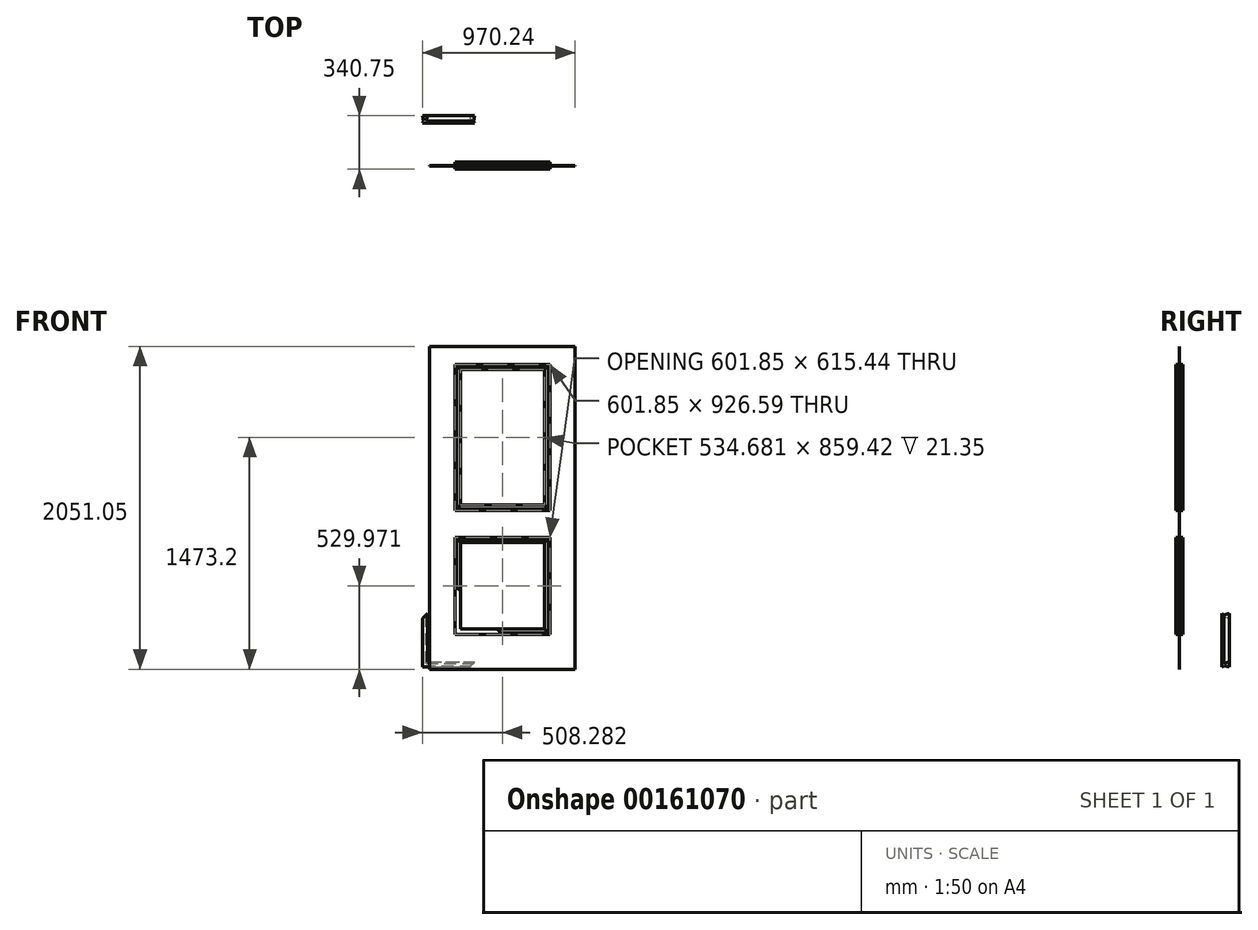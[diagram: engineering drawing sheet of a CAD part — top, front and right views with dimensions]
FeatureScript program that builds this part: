
annotation { "Feature Type Name" : "Feature", "Feature Type Description" : "" }
export const myFeature = defineFeature(function(context is Context, id is Id, definition is map)
    precondition{}
    {
        {
            var Q0;
            Q0=qCreatedBy(makeId("Front.planeOp"),FACE);
            var sketch = newSketch(context, id + "F0", { "sketchPlane" : qUnion([Q0])});
            skLineSegment(sketch, "E0.bottom", {"start": v(0, 0) * mm, "end": v(923.92, 0) * mm});
            skLineSegment(sketch, "E0.top", {"start": v(0, 2051.05) * mm, "end": v(923.92, 2051.05) * mm});
            skLineSegment(sketch, "E0.left", {"start": v(0, 0) * mm, "end": v(0, 2051.05) * mm});
            skLineSegment(sketch, "E0.right", {"start": v(923.93, 0) * mm, "end": v(923.92, 2051.05) * mm});
            skLineSegment(sketch, "E1.bottom", {"start": v(762.89, 1936.5) * mm, "end": v(161.04, 1936.5) * mm});
            skLineSegment(sketch, "E1.top", {"start": v(762.89, 1009.9) * mm, "end": v(161.04, 1009.9) * mm});
            skLineSegment(sketch, "E1.left", {"start": v(762.89, 1936.5) * mm, "end": v(762.89, 1009.9) * mm});
            skLineSegment(sketch, "E1.right", {"start": v(161.04, 1936.5) * mm, "end": v(161.04, 1009.9) * mm});
            skLineSegment(sketch, "E2.bottom", {"start": v(161.04, 837.7) * mm, "end": v(762.89, 837.7) * mm});
            skLineSegment(sketch, "E2.top", {"start": v(161.04, 222.25) * mm, "end": v(762.89, 222.25) * mm});
            skLineSegment(sketch, "E2.left", {"start": v(161.04, 837.7) * mm, "end": v(161.04, 222.25) * mm});
            skLineSegment(sketch, "E2.right", {"start": v(762.89, 837.7) * mm, "end": v(762.89, 222.25) * mm});
            skSolve(sketch);
        }
        {
            var Q0;
            Q0=qSketchRegion(id+"F0",true);
            extrude(context, id + "F1", {"entities" : qUnion([Q0]), "depth" : ((1 + 3 / 4) / 2) * mm, "hasSecondDirection" : true, "secondDirectionOppositeDirection" : true, "secondDirectionDepth" : ((1 + 3 / 4) / 2) * mm});
        }
        {
            var Q0;
            Q0=qCreatedBy(makeId("Front.planeOp"),FACE);
            var sketch = newSketch(context, id + "F2", { "sketchPlane" : qUnion([Q0])});
            skLineSegment(sketch, "E3.0", {"start": v(762.89, 837.7) * mm, "end": v(762.89, 222.25) * mm});
            skLineSegment(sketch, "E4.0", {"start": v(161.04, 222.25) * mm, "end": v(762.89, 222.25) * mm});
            skLineSegment(sketch, "E5.0", {"start": v(161.04, 837.7) * mm, "end": v(161.04, 222.25) * mm});
            skLineSegment(sketch, "E6.0", {"start": v(161.04, 837.7) * mm, "end": v(762.89, 837.7) * mm});
            skLineSegment(sketch, "E7.0", {"start": v(762.89, 1009.9) * mm, "end": v(161.04, 1009.9) * mm});
            skLineSegment(sketch, "E8.0", {"start": v(762.89, 1936.5) * mm, "end": v(762.89, 1009.9) * mm});
            skLineSegment(sketch, "E9.0", {"start": v(161.04, 1936.5) * mm, "end": v(161.04, 1009.9) * mm});
            skLineSegment(sketch, "E10.0", {"start": v(762.89, 1936.5) * mm, "end": v(161.04, 1936.5) * mm});
            skLineSegment(sketch, "E11", {"start": v(461.96, 1936.5) * mm, "end": v(461.96, 222.25) * mm});
            skLineSegment(sketch, "E12", {"start": v(161.04, 1473.2) * mm, "end": v(762.89, 1473.2) * mm});
            skLineSegment(sketch, "E13", {"start": v(161.04, 529.97) * mm, "end": v(762.89, 529.97) * mm});
            skLineSegment(sketch, "E14", {"start": v(161.04, 1936.5) * mm, "end": v(186.44, 1911.1) * mm});
            skLineSegment(sketch, "E15", {"start": v(161.04, 837.7) * mm, "end": v(186.44, 812.3) * mm});
            skLineSegment(sketch, "E16", {"start": v(762.89, 1936.5) * mm, "end": v(737.49, 1911.1) * mm});
            skLineSegment(sketch, "E17", {"start": v(161.04, 1009.9) * mm, "end": v(186.44, 1035.3) * mm});
            skLineSegment(sketch, "E18", {"start": v(762.89, 1009.9) * mm, "end": v(737.49, 1035.3) * mm});
            skLineSegment(sketch, "E19", {"start": v(762.89, 222.25) * mm, "end": v(737.49, 247.65) * mm});
            skLineSegment(sketch, "E20", {"start": v(762.89, 837.7) * mm, "end": v(737.49, 812.3) * mm});
            skLineSegment(sketch, "E21", {"start": v(161.04, 222.25) * mm, "end": v(186.44, 247.65) * mm});
            skSolve(sketch);
        }
        {
            var Q0;
            Q0=qCreatedBy(makeId("Front.planeOp"),FACE);
            var sketch = newSketch(context, id + "F3", { "sketchPlane" : qUnion([Q0])});
            skPoint(sketch, "E22.0", {"position": v(161.04, 1473.2) * mm});
            skPoint(sketch, "E23.0", {"position": v(762.89, 1473.2) * mm});
            skPoint(sketch, "E24.0", {"position": v(461.96, 1936.5) * mm});
            skLineSegment(sketch, "E25.0", {"start": v(461.96, 1936.5) * mm, "end": v(461.96, 222.25) * mm});
            skPoint(sketch, "E26.0", {"position": v(762.89, 1009.9) * mm});
            skPoint(sketch, "E27.0", {"position": v(161.04, 1009.9) * mm});
            skPoint(sketch, "E28.0", {"position": v(762.89, 1936.5) * mm});
            skPoint(sketch, "E29.0", {"position": v(161.04, 1936.5) * mm});
            skPoint(sketch, "E30.0", {"position": v(161.04, 837.7) * mm});
            skPoint(sketch, "E31.0", {"position": v(762.89, 837.7) * mm});
            skPoint(sketch, "E32.0", {"position": v(762.89, 529.97) * mm});
            skPoint(sketch, "E33.0", {"position": v(762.89, 222.25) * mm});
            skPoint(sketch, "E34.0", {"position": v(161.04, 222.25) * mm});
            skPoint(sketch, "E35.0", {"position": v(161.04, 529.97) * mm});
            skLineSegment(sketch, "E36", {"start": v(161.04, 837.7) * mm, "end": v(461.96, 837.7) * mm});
            skLineSegment(sketch, "E37", {"start": v(461.96, 837.7) * mm, "end": v(762.89, 837.7) * mm});
            skLineSegment(sketch, "E38", {"start": v(762.89, 837.7) * mm, "end": v(762.89, 529.97) * mm});
            skLineSegment(sketch, "E39", {"start": v(762.89, 529.97) * mm, "end": v(762.89, 222.25) * mm});
            skLineSegment(sketch, "E40", {"start": v(762.89, 222.25) * mm, "end": v(461.96, 222.25) * mm});
            skLineSegment(sketch, "E41", {"start": v(461.96, 222.25) * mm, "end": v(161.04, 222.25) * mm});
            skLineSegment(sketch, "E42", {"start": v(161.04, 222.25) * mm, "end": v(161.04, 529.97) * mm});
            skLineSegment(sketch, "E43", {"start": v(161.04, 529.97) * mm, "end": v(161.04, 837.7) * mm});
            skLineSegment(sketch, "E44", {"start": v(161.04, 1936.5) * mm, "end": v(461.96, 1936.5) * mm});
            skLineSegment(sketch, "E45", {"start": v(461.96, 1936.5) * mm, "end": v(762.89, 1936.5) * mm});
            skLineSegment(sketch, "E46", {"start": v(762.89, 1936.5) * mm, "end": v(762.89, 1473.2) * mm});
            skLineSegment(sketch, "E47", {"start": v(762.89, 1473.2) * mm, "end": v(762.89, 1009.9) * mm});
            skLineSegment(sketch, "E48", {"start": v(762.89, 1009.9) * mm, "end": v(461.96, 1009.9) * mm});
            skLineSegment(sketch, "E49", {"start": v(461.96, 1009.9) * mm, "end": v(161.04, 1009.9) * mm});
            skLineSegment(sketch, "E50", {"start": v(161.04, 1009.9) * mm, "end": v(161.04, 1473.2) * mm});
            skLineSegment(sketch, "E51", {"start": v(161.04, 1473.2) * mm, "end": v(161.04, 1936.5) * mm});
            skSolve(sketch);
        }
        {
            var Q0;
            Q0=sQuery(id+"F2.wireOp",VERTEX,"E14.end");
            var Q1;
            Q1=sQuery(id+"F3.wireOp",VERTEX,"E29.0");
            var Q2;
            Q2=makeQuery(id+"F1.opExtrude","CAP_VERTEX",VERTEX,{"disambiguationData":[OSD([sQuery(id+"F0.wireOp",EDGE,"E1.bottom"),sQuery(id+"F0.wireOp",EDGE,"E1.right")])],"isStart":false});
            cPlane(context, id + "F4", {"entities" : qUnion([Q0, Q1, Q2]), "cplaneType" : CPlaneType.THREE_POINT, "offset" : 25.4 * mm, "width" : 152.4 * mm, "height" : 152.4 * mm});
        }
        {
            var Q0;
            Q0=sQuery(id+"F3.wireOp",VERTEX,"E28.0");
            var Q1;
            Q1=sQuery(id+"F2.wireOp",VERTEX,"E16.end");
            var Q2;
            Q2=makeQuery(id+"F1.opExtrude","CAP_VERTEX",VERTEX,{"disambiguationData":[OSD([sQuery(id+"F0.wireOp",EDGE,"E1.bottom"),sQuery(id+"F0.wireOp",EDGE,"E1.left")])],"isStart":false});
            cPlane(context, id + "F5", {"entities" : qUnion([Q0, Q1, Q2]), "cplaneType" : CPlaneType.THREE_POINT, "offset" : 25.4 * mm, "width" : 152.4 * mm, "height" : 152.4 * mm});
        }
        {
            var Q0;
            Q0=sQuery(id+"F3.wireOp",VERTEX,"E26.0");
            var Q1;
            Q1=sQuery(id+"F2.wireOp",VERTEX,"E18.end");
            var Q2;
            Q2=makeQuery(id+"F1.opExtrude","CAP_VERTEX",VERTEX,{"disambiguationData":[OSD([sQuery(id+"F0.wireOp",EDGE,"E1.top"),sQuery(id+"F0.wireOp",EDGE,"E1.left")])],"isStart":false});
            cPlane(context, id + "F6", {"entities" : qUnion([Q0, Q1, Q2]), "cplaneType" : CPlaneType.THREE_POINT, "offset" : 25.4 * mm, "width" : 152.4 * mm, "height" : 152.4 * mm});
        }
        {
            var Q0;
            Q0=sQuery(id+"F3.wireOp",VERTEX,"E27.0");
            var Q1;
            Q1=sQuery(id+"F2.wireOp",VERTEX,"E17.end");
            var Q2;
            Q2=makeQuery(id+"F1.opExtrude","CAP_VERTEX",VERTEX,{"disambiguationData":[OSD([sQuery(id+"F0.wireOp",EDGE,"E1.top"),sQuery(id+"F0.wireOp",EDGE,"E1.right")])],"isStart":false});
            cPlane(context, id + "F7", {"entities" : qUnion([Q0, Q1, Q2]), "cplaneType" : CPlaneType.THREE_POINT, "offset" : 25.4 * mm, "width" : 152.4 * mm, "height" : 152.4 * mm});
        }
        {
            var Q0;
            Q0=sQuery(id+"F2.wireOp",VERTEX,"E15.end");
            var Q1;
            Q1=sQuery(id+"F3.wireOp",VERTEX,"E30.0");
            var Q2;
            Q2=makeQuery(id+"F1.opExtrude","CAP_VERTEX",VERTEX,{"disambiguationData":[OSD([sQuery(id+"F0.wireOp",EDGE,"E2.bottom"),sQuery(id+"F0.wireOp",EDGE,"E2.left")])],"isStart":false});
            cPlane(context, id + "F8", {"entities" : qUnion([Q0, Q1, Q2]), "cplaneType" : CPlaneType.THREE_POINT, "offset" : 25.4 * mm, "width" : 152.4 * mm, "height" : 152.4 * mm});
        }
        {
            var Q0;
            Q0=sQuery(id+"F2.wireOp",VERTEX,"E21.end");
            var Q1;
            Q1=sQuery(id+"F3.wireOp",VERTEX,"E34.0");
            var Q2;
            Q2=makeQuery(id+"F1.opExtrude","CAP_VERTEX",VERTEX,{"disambiguationData":[OSD([sQuery(id+"F0.wireOp",EDGE,"E2.top"),sQuery(id+"F0.wireOp",EDGE,"E2.left")])],"isStart":false});
            cPlane(context, id + "F9", {"entities" : qUnion([Q0, Q1, Q2]), "cplaneType" : CPlaneType.THREE_POINT, "offset" : 25.4 * mm, "width" : 152.4 * mm, "height" : 152.4 * mm});
        }
        {
            var Q0;
            Q0=sQuery(id+"F2.wireOp",VERTEX,"E19.end");
            var Q1;
            Q1=sQuery(id+"F3.wireOp",VERTEX,"E33.0");
            var Q2;
            Q2=makeQuery(id+"F1.opExtrude","CAP_VERTEX",VERTEX,{"disambiguationData":[OSD([sQuery(id+"F0.wireOp",EDGE,"E2.top"),sQuery(id+"F0.wireOp",EDGE,"E2.right")])],"isStart":false});
            cPlane(context, id + "F10", {"entities" : qUnion([Q0, Q1, Q2]), "cplaneType" : CPlaneType.THREE_POINT, "offset" : 25.4 * mm, "width" : 152.4 * mm, "height" : 152.4 * mm});
        }
        {
            var Q0;
            Q0=sQuery(id+"F3.wireOp",VERTEX,"E31.0");
            var Q1;
            Q1=sQuery(id+"F2.wireOp",VERTEX,"E20.end");
            var Q2;
            Q2=makeQuery(id+"F1.opExtrude","CAP_VERTEX",VERTEX,{"disambiguationData":[OSD([sQuery(id+"F0.wireOp",EDGE,"E2.bottom"),sQuery(id+"F0.wireOp",EDGE,"E2.right")])],"isStart":false});
            cPlane(context, id + "F11", {"entities" : qUnion([Q0, Q1, Q2]), "cplaneType" : CPlaneType.THREE_POINT, "offset" : 25.4 * mm, "width" : 152.4 * mm, "height" : 152.4 * mm});
        }
        {
            var Q0;
            Q0=makeQuery(id+"F1.opExtrude","SWEPT_FACE",FACE,{"disambiguationData":[OSD([sQuery(id+"F0.wireOp",EDGE,"E2.top")])]});
            var sketch = newSketch(context, id + "F12", { "sketchPlane" : qUnion([Q0])});
            skLineSegment(sketch, "E52.0", {"start": v(161.04, -22.23) * mm, "end": v(161.04, 22.23) * mm});
            skLineSegment(sketch, "E53.0", {"start": v(762.89, -22.23) * mm, "end": v(762.89, 22.23) * mm});
            skLineSegment(sketch, "E54", {"start": v(161.04, -22.22) * mm, "end": v(179, -11.3) * mm});
            skLineSegment(sketch, "E55", {"start": v(179, -11.3) * mm, "end": v(228.2, -22.23) * mm});
            skLineSegment(sketch, "E56", {"start": v(228.2, -22.23) * mm, "end": v(228.2, 22.23) * mm});
            skLineSegment(sketch, "E57", {"start": v(228.2, 22.22) * mm, "end": v(179, 11.3) * mm});
            skLineSegment(sketch, "E58", {"start": v(179, 11.3) * mm, "end": v(161.04, 22.22) * mm});
            skLineSegment(sketch, "E59", {"start": v(762.89, -22.23) * mm, "end": v(744.93, -11.3) * mm});
            skLineSegment(sketch, "E60", {"start": v(744.93, -11.3) * mm, "end": v(695.72, -22.23) * mm});
            skLineSegment(sketch, "E61", {"start": v(695.72, -22.23) * mm, "end": v(695.72, 22.23) * mm});
            skLineSegment(sketch, "E62", {"start": v(695.72, 22.22) * mm, "end": v(744.93, 11.3) * mm});
            skLineSegment(sketch, "E63", {"start": v(744.93, 11.3) * mm, "end": v(762.89, 22.23) * mm});
            skSolve(sketch);
        }
        {
            var Q0;
            Q0=makeQuery(id+"F1.opExtrude","SWEPT_FACE",FACE,{"disambiguationData":[OSD([sQuery(id+"F0.wireOp",EDGE,"E2.bottom")])]});
            var sketch = newSketch(context, id + "F13", { "sketchPlane" : qUnion([Q0])});
            skLineSegment(sketch, "E64.0", {"start": v(179, 11.3) * mm, "end": v(228.2, 22.23) * mm});
            skLineSegment(sketch, "E64.1", {"start": v(161.04, 22.22) * mm, "end": v(179, 11.3) * mm});
            skLineSegment(sketch, "E64.2", {"start": v(228.2, -22.22) * mm, "end": v(179, -11.3) * mm});
            skLineSegment(sketch, "E64.3", {"start": v(161.04, 22.23) * mm, "end": v(161.04, -22.23) * mm});
            skLineSegment(sketch, "E64.4", {"start": v(179, -11.3) * mm, "end": v(161.04, -22.22) * mm});
            skLineSegment(sketch, "E64.5", {"start": v(228.2, 22.23) * mm, "end": v(228.2, -22.23) * mm});
            skLineSegment(sketch, "E64.7", {"start": v(161.04, 22.23) * mm, "end": v(161.04, -22.23) * mm});
            skLineSegment(sketch, "E64.8", {"start": v(161.04, -22.23) * mm, "end": v(762.89, -22.23) * mm});
            skLineSegment(sketch, "E64.10", {"start": v(161.04, 22.23) * mm, "end": v(762.89, 22.23) * mm});
            skLineSegment(sketch, "E65.0", {"start": v(744.93, -11.3) * mm, "end": v(762.89, -22.23) * mm});
            skLineSegment(sketch, "E65.1", {"start": v(695.72, -22.22) * mm, "end": v(744.93, -11.3) * mm});
            skLineSegment(sketch, "E65.2", {"start": v(744.93, 11.3) * mm, "end": v(695.72, 22.23) * mm});
            skLineSegment(sketch, "E65.3", {"start": v(695.72, 22.23) * mm, "end": v(695.72, -22.23) * mm});
            skLineSegment(sketch, "E65.4", {"start": v(762.89, 22.23) * mm, "end": v(762.89, -22.23) * mm});
            skLineSegment(sketch, "E65.5", {"start": v(762.89, 22.23) * mm, "end": v(744.93, 11.3) * mm});
            skLineSegment(sketch, "E65.6", {"start": v(762.89, 22.23) * mm, "end": v(762.89, -22.23) * mm});
            skSolve(sketch);
        }
        {
            var Q0;
            Q0=makeQuery(id+"F1.opExtrude","SWEPT_FACE",FACE,{"disambiguationData":[OSD([sQuery(id+"F0.wireOp",EDGE,"E1.top")])]});
            var sketch = newSketch(context, id + "F14", { "sketchPlane" : qUnion([Q0])});
            skLineSegment(sketch, "E66.0", {"start": v(179, -11.3) * mm, "end": v(228.2, -22.23) * mm});
            skLineSegment(sketch, "E66.1", {"start": v(161.04, -22.22) * mm, "end": v(179, -11.3) * mm});
            skLineSegment(sketch, "E66.2", {"start": v(228.2, 22.22) * mm, "end": v(179, 11.3) * mm});
            skLineSegment(sketch, "E66.3", {"start": v(161.04, -22.23) * mm, "end": v(161.04, 22.23) * mm});
            skLineSegment(sketch, "E66.4", {"start": v(228.2, -22.23) * mm, "end": v(228.2, 22.23) * mm});
            skLineSegment(sketch, "E66.6", {"start": v(161.04, -22.23) * mm, "end": v(762.89, -22.23) * mm});
            skLineSegment(sketch, "E66.7", {"start": v(161.04, -22.23) * mm, "end": v(161.04, 22.23) * mm});
            skLineSegment(sketch, "E66.8", {"start": v(161.04, 22.23) * mm, "end": v(762.89, 22.23) * mm});
            skLineSegment(sketch, "E66.10", {"start": v(179, 11.3) * mm, "end": v(161.04, 22.22) * mm});
            skLineSegment(sketch, "E67.0", {"start": v(744.93, 11.3) * mm, "end": v(762.89, 22.23) * mm});
            skLineSegment(sketch, "E67.1", {"start": v(695.72, 22.22) * mm, "end": v(744.93, 11.3) * mm});
            skLineSegment(sketch, "E67.2", {"start": v(744.93, -11.3) * mm, "end": v(695.72, -22.23) * mm});
            skLineSegment(sketch, "E67.3", {"start": v(695.72, -22.23) * mm, "end": v(695.72, 22.23) * mm});
            skLineSegment(sketch, "E67.4", {"start": v(762.89, -22.23) * mm, "end": v(762.89, 22.23) * mm});
            skLineSegment(sketch, "E67.5", {"start": v(762.89, -22.23) * mm, "end": v(762.89, 22.23) * mm});
            skLineSegment(sketch, "E67.6", {"start": v(762.89, -22.23) * mm, "end": v(744.93, -11.3) * mm});
            skSolve(sketch);
        }
        {
            var Q0;
            Q0=makeQuery(id+"F1.opExtrude","SWEPT_FACE",FACE,{"disambiguationData":[OSD([sQuery(id+"F0.wireOp",EDGE,"E1.bottom")])]});
            var sketch = newSketch(context, id + "F15", { "sketchPlane" : qUnion([Q0])});
            skLineSegment(sketch, "E68.0", {"start": v(179, 11.3) * mm, "end": v(228.2, 22.23) * mm});
            skLineSegment(sketch, "E68.1", {"start": v(161.04, 22.22) * mm, "end": v(179, 11.3) * mm});
            skLineSegment(sketch, "E68.2", {"start": v(228.2, -22.22) * mm, "end": v(179, -11.3) * mm});
            skLineSegment(sketch, "E68.3", {"start": v(161.04, 22.23) * mm, "end": v(161.04, -22.23) * mm});
            skLineSegment(sketch, "E68.4", {"start": v(179, -11.3) * mm, "end": v(161.04, -22.22) * mm});
            skLineSegment(sketch, "E68.5", {"start": v(228.2, 22.23) * mm, "end": v(228.2, -22.23) * mm});
            skLineSegment(sketch, "E68.9", {"start": v(161.04, 22.23) * mm, "end": v(161.04, -22.23) * mm});
            skLineSegment(sketch, "E69.0", {"start": v(695.72, -22.22) * mm, "end": v(744.93, -11.3) * mm});
            skLineSegment(sketch, "E69.1", {"start": v(744.93, 11.3) * mm, "end": v(695.72, 22.23) * mm});
            skLineSegment(sketch, "E69.2", {"start": v(695.72, 22.23) * mm, "end": v(695.72, -22.23) * mm});
            skLineSegment(sketch, "E69.3", {"start": v(762.89, 22.23) * mm, "end": v(762.89, -22.23) * mm});
            skLineSegment(sketch, "E69.4", {"start": v(762.89, 22.23) * mm, "end": v(744.93, 11.3) * mm});
            skLineSegment(sketch, "E69.5", {"start": v(762.89, 22.23) * mm, "end": v(762.89, -22.23) * mm});
            skLineSegment(sketch, "E69.6", {"start": v(744.93, -11.3) * mm, "end": v(762.89, -22.23) * mm});
            skSolve(sketch);
        }
        {
            var Q0;
            Q0=qCreatedBy(id+"F4.planeOp",FACE);
            var sketch = newSketch(context, id + "F16", { "sketchPlane" : qUnion([Q0])});
            skLineSegment(sketch, "E70.0", {"start": v(22.23, 1255.44) * mm, "end": v(-22.23, 1255.44) * mm});
            skLineSegment(sketch, "E71.0", {"start": v(22.22, 1255.44) * mm, "end": v(11.3, 1242.74) * mm});
            skLineSegment(sketch, "E72.0", {"start": v(11.3, 1242.74) * mm, "end": v(22.23, 1207.94) * mm});
            skLineSegment(sketch, "E73.0", {"start": v(22.23, 1207.94) * mm, "end": v(-22.23, 1207.94) * mm});
            skLineSegment(sketch, "E74.0", {"start": v(-22.22, 1207.94) * mm, "end": v(-11.3, 1242.74) * mm});
            skLineSegment(sketch, "E75.0", {"start": v(-11.3, 1242.74) * mm, "end": v(-22.22, 1255.44) * mm});
            skSolve(sketch);
        }
        {
            var Q0;
            Q0=qCreatedBy(id+"F5.planeOp",FACE);
            var sketch = newSketch(context, id + "F17", { "sketchPlane" : qUnion([Q0])});
            skLineSegment(sketch, "E76.0", {"start": v(-22.23, 1908.75) * mm, "end": v(22.23, 1908.75) * mm});
            skLineSegment(sketch, "E77.0", {"start": v(-22.22, 1908.75) * mm, "end": v(-11.3, 1896.05) * mm});
            skLineSegment(sketch, "E78.0", {"start": v(11.3, 1896.05) * mm, "end": v(22.23, 1908.75) * mm});
            skLineSegment(sketch, "E79.0", {"start": v(22.23, 1861.26) * mm, "end": v(11.3, 1896.05) * mm});
            skLineSegment(sketch, "E80.0", {"start": v(-11.3, 1896.05) * mm, "end": v(-22.22, 1861.26) * mm});
            skLineSegment(sketch, "E81.0", {"start": v(-22.23, 1861.26) * mm, "end": v(22.23, 1861.26) * mm});
            skSolve(sketch);
        }
        {
            var Q0;
            Q0=qCreatedBy(id+"F6.planeOp",FACE);
            var sketch = newSketch(context, id + "F18", { "sketchPlane" : qUnion([Q0])});
            skLineSegment(sketch, "E82.0", {"start": v(22.23, 174.67) * mm, "end": v(-22.22, 174.67) * mm});
            skLineSegment(sketch, "E83.0", {"start": v(22.23, 174.67) * mm, "end": v(11.3, 187.37) * mm});
            skLineSegment(sketch, "E84.0", {"start": v(-11.3, 187.37) * mm, "end": v(-22.22, 174.67) * mm});
            skLineSegment(sketch, "E85.0", {"start": v(-22.22, 222.16) * mm, "end": v(-11.3, 187.37) * mm});
            skLineSegment(sketch, "E86.0", {"start": v(11.3, 187.37) * mm, "end": v(22.23, 222.16) * mm});
            skLineSegment(sketch, "E87.0", {"start": v(22.23, 222.16) * mm, "end": v(-22.22, 222.16) * mm});
            skSolve(sketch);
        }
        {
            var Q0;
            Q0=qCreatedBy(id+"F7.planeOp",FACE);
            var sketch = newSketch(context, id + "F19", { "sketchPlane" : qUnion([Q0])});
            skLineSegment(sketch, "E88.0", {"start": v(22.23, 827.98) * mm, "end": v(-22.23, 827.98) * mm});
            skLineSegment(sketch, "E89.0", {"start": v(22.23, 827.98) * mm, "end": v(11.3, 840.68) * mm});
            skLineSegment(sketch, "E90.0", {"start": v(-11.3, 840.68) * mm, "end": v(-22.23, 827.98) * mm});
            skLineSegment(sketch, "E91.0", {"start": v(-22.23, 875.48) * mm, "end": v(-11.3, 840.68) * mm});
            skLineSegment(sketch, "E92.0", {"start": v(11.3, 840.68) * mm, "end": v(22.22, 875.48) * mm});
            skLineSegment(sketch, "E93.0", {"start": v(22.23, 875.48) * mm, "end": v(-22.23, 875.48) * mm});
            skSolve(sketch);
        }
        {
            var Q0;
            Q0=qCreatedBy(id+"F8.planeOp",FACE);
            var sketch = newSketch(context, id + "F20", { "sketchPlane" : qUnion([Q0])});
            skLineSegment(sketch, "E94.0", {"start": v(22.23, 478.47) * mm, "end": v(-22.23, 478.47) * mm});
            skLineSegment(sketch, "E95.0", {"start": v(-11.3, 465.77) * mm, "end": v(-22.22, 478.47) * mm});
            skLineSegment(sketch, "E96.0", {"start": v(22.23, 478.47) * mm, "end": v(11.3, 465.77) * mm});
            skLineSegment(sketch, "E97.0", {"start": v(-22.22, 430.97) * mm, "end": v(-11.3, 465.77) * mm});
            skLineSegment(sketch, "E98.0", {"start": v(11.3, 465.77) * mm, "end": v(22.23, 430.97) * mm});
            skLineSegment(sketch, "E99.0", {"start": v(22.23, 430.97) * mm, "end": v(-22.23, 430.97) * mm});
            skSolve(sketch);
        }
        {
            var Q0;
            Q0=qCreatedBy(id+"F9.planeOp",FACE);
            var sketch = newSketch(context, id + "F21", { "sketchPlane" : qUnion([Q0])});
            skLineSegment(sketch, "E100.0", {"start": v(271.02, 22.23) * mm, "end": v(271.02, -22.23) * mm});
            skLineSegment(sketch, "E101.0", {"start": v(271.02, 22.23) * mm, "end": v(283.72, 11.3) * mm});
            skLineSegment(sketch, "E102.0", {"start": v(283.72, -11.3) * mm, "end": v(271.02, -22.23) * mm});
            skLineSegment(sketch, "E103.0", {"start": v(318.52, -22.22) * mm, "end": v(283.72, -11.3) * mm});
            skLineSegment(sketch, "E104.0", {"start": v(283.72, 11.3) * mm, "end": v(318.52, 22.23) * mm});
            skLineSegment(sketch, "E105.0", {"start": v(318.52, 22.23) * mm, "end": v(318.52, -22.23) * mm});
            skSolve(sketch);
        }
        {
            var Q0;
            Q0=qCreatedBy(id+"F10.planeOp",FACE);
            var sketch = newSketch(context, id + "F22", { "sketchPlane" : qUnion([Q0])});
            skLineSegment(sketch, "E106.0", {"start": v(-22.23, -382.29) * mm, "end": v(22.23, -382.29) * mm});
            skLineSegment(sketch, "E107.0", {"start": v(11.3, -369.59) * mm, "end": v(22.23, -382.29) * mm});
            skLineSegment(sketch, "E108.0", {"start": v(-22.22, -382.29) * mm, "end": v(-11.3, -369.59) * mm});
            skLineSegment(sketch, "E109.0", {"start": v(-11.3, -369.59) * mm, "end": v(-22.23, -334.8) * mm});
            skLineSegment(sketch, "E110.0", {"start": v(22.22, -334.8) * mm, "end": v(11.3, -369.59) * mm});
            skLineSegment(sketch, "E111.0", {"start": v(-22.23, -334.8) * mm, "end": v(22.23, -334.8) * mm});
            skSolve(sketch);
        }
        {
            var Q0;
            Q0=qCreatedBy(id+"F11.planeOp",FACE);
            var sketch = newSketch(context, id + "F23", { "sketchPlane" : qUnion([Q0])});
            skLineSegment(sketch, "E112.0", {"start": v(-22.23, 1131.78) * mm, "end": v(22.23, 1131.78) * mm});
            skLineSegment(sketch, "E113.0", {"start": v(-22.22, 1131.78) * mm, "end": v(-11.3, 1119.08) * mm});
            skLineSegment(sketch, "E114.0", {"start": v(-11.3, 1119.08) * mm, "end": v(-22.22, 1084.28) * mm});
            skLineSegment(sketch, "E115.0", {"start": v(-22.23, 1084.28) * mm, "end": v(22.23, 1084.28) * mm});
            skLineSegment(sketch, "E116.0", {"start": v(22.23, 1084.28) * mm, "end": v(11.3, 1119.08) * mm});
            skLineSegment(sketch, "E117.0", {"start": v(11.3, 1119.08) * mm, "end": v(22.23, 1131.78) * mm});
            skSolve(sketch);
        }
        {
            var Q0;
            Q0 = qSketchRegion(id + "F16", true);
            var Q1;
            Q1=sQuery(id+"F3.wireOp",EDGE,"E51");
            sweep(context, id + "F24", {"operationType" : NewBodyOperationType.ADD, "profiles" : qUnion([Q0]), "path" : qUnion([Q1])});
        }
        {
            var Q0;
            Q0 = qSketchRegion(id + "F16", true);
            var Q1;
            Q1=sQuery(id+"F3.wireOp",EDGE,"E44");
            sweep(context, id + "F25", {"operationType" : NewBodyOperationType.ADD, "profiles" : qUnion([Q0]), "path" : qUnion([Q1])});
        }
        {
            var Q0;
            Q0 = qSketchRegion(id + "F17", true);
            var Q1;
            Q1=sQuery(id+"F3.wireOp",EDGE,"E45");
            sweep(context, id + "F26", {"operationType" : NewBodyOperationType.ADD, "profiles" : qUnion([Q0]), "path" : qUnion([Q1])});
        }
        {
            var Q0;
            Q0 = qSketchRegion(id + "F17", true);
            var Q1;
            Q1=sQuery(id+"F3.wireOp",EDGE,"E46");
            sweep(context, id + "F27", {"operationType" : NewBodyOperationType.ADD, "profiles" : qUnion([Q0]), "path" : qUnion([Q1])});
        }
        {
            var Q0;
            Q0 = qSketchRegion(id + "F18", true);
            var Q1;
            Q1=sQuery(id+"F3.wireOp",EDGE,"E47");
            sweep(context, id + "F28", {"operationType" : NewBodyOperationType.ADD, "profiles" : qUnion([Q0]), "path" : qUnion([Q1])});
        }
        {
            var Q0;
            Q0 = qSketchRegion(id + "F18", true);
            var Q1;
            Q1=sQuery(id+"F3.wireOp",EDGE,"E48");
            sweep(context, id + "F29", {"operationType" : NewBodyOperationType.ADD, "profiles" : qUnion([Q0]), "path" : qUnion([Q1])});
        }
        {
            var Q0;
            Q0 = qSketchRegion(id + "F19", true);
            var Q1;
            Q1=sQuery(id+"F3.wireOp",EDGE,"E49");
            sweep(context, id + "F30", {"operationType" : NewBodyOperationType.ADD, "profiles" : qUnion([Q0]), "path" : qUnion([Q1])});
        }
        {
            var Q0;
            Q0 = qSketchRegion(id + "F19", true);
            var Q1;
            Q1=sQuery(id+"F3.wireOp",EDGE,"E50");
            sweep(context, id + "F31", {"operationType" : NewBodyOperationType.ADD, "profiles" : qUnion([Q0]), "path" : qUnion([Q1])});
        }
        {
            var Q0;
            Q0 = qSketchRegion(id + "F20", true);
            var Q1;
            Q1=sQuery(id+"F3.wireOp",EDGE,"E36");
            sweep(context, id + "F32", {"operationType" : NewBodyOperationType.ADD, "profiles" : qUnion([Q0]), "path" : qUnion([Q1])});
        }
        {
            var Q0;
            Q0 = qSketchRegion(id + "F20", true);
            var Q1;
            Q1=sQuery(id+"F3.wireOp",EDGE,"E43");
            sweep(context, id + "F33", {"operationType" : NewBodyOperationType.ADD, "profiles" : qUnion([Q0]), "path" : qUnion([Q1])});
        }
        {
            var Q0;
            Q0 = qSketchRegion(id + "F21", true);
            var Q1;
            Q1=sQuery(id+"F3.wireOp",EDGE,"E42");
            sweep(context, id + "F34", {"operationType" : NewBodyOperationType.ADD, "profiles" : qUnion([Q0]), "path" : qUnion([Q1])});
        }
        {
            var Q0;
            Q0 = qSketchRegion(id + "F21", true);
            var Q1;
            Q1=sQuery(id+"F3.wireOp",EDGE,"E41");
            sweep(context, id + "F35", {"operationType" : NewBodyOperationType.ADD, "profiles" : qUnion([Q0]), "path" : qUnion([Q1])});
        }
        {
            var Q0;
            Q0 = qSketchRegion(id + "F22", true);
            var Q1;
            Q1=sQuery(id+"F3.wireOp",EDGE,"E40");
            sweep(context, id + "F36", {"operationType" : NewBodyOperationType.ADD, "profiles" : qUnion([Q0]), "path" : qUnion([Q1])});
        }
        {
            var Q0;
            Q0 = qSketchRegion(id + "F22", true);
            var Q1;
            Q1=sQuery(id+"F3.wireOp",EDGE,"E39");
            sweep(context, id + "F37", {"operationType" : NewBodyOperationType.ADD, "profiles" : qUnion([Q0]), "path" : qUnion([Q1])});
        }
        {
            var Q0;
            Q0 = qSketchRegion(id + "F23", true);
            var Q1;
            Q1=sQuery(id+"F3.wireOp",EDGE,"E38");
            sweep(context, id + "F38", {"operationType" : NewBodyOperationType.ADD, "profiles" : qUnion([Q0]), "path" : qUnion([Q1])});
        }
        {
            var Q0;
            Q0 = qSketchRegion(id + "F23", true);
            var Q1;
            Q1=sQuery(id+"F3.wireOp",EDGE,"E37");
            sweep(context, id + "F39", {"operationType" : NewBodyOperationType.ADD, "profiles" : qUnion([Q0]), "path" : qUnion([Q1])});
        }
        {
            var Q0;
            Q0=qCreatedBy(makeId("Front.planeOp"),FACE);
            var sketch = newSketch(context, id + "F40", { "sketchPlane" : qUnion([Q0])});
            skLineSegment(sketch, "E118.0", {"start": v(194.62, 1902.9) * mm, "end": v(729.3, 1902.9) * mm});
            skLineSegment(sketch, "E119.0", {"start": v(729.3, 1902.9) * mm, "end": v(729.3, 1043.5) * mm});
            skLineSegment(sketch, "E120.0", {"start": v(729.3, 1043.5) * mm, "end": v(194.62, 1043.5) * mm});
            skLineSegment(sketch, "E121.0", {"start": v(194.62, 1902.9) * mm, "end": v(194.62, 1043.5) * mm});
            skLineSegment(sketch, "E122.0", {"start": v(194.62, 804.1) * mm, "end": v(729.3, 804.1) * mm});
            skLineSegment(sketch, "E123.0", {"start": v(194.62, 804.1) * mm, "end": v(194.62, 255.84) * mm});
            skLineSegment(sketch, "E124.0", {"start": v(194.62, 255.84) * mm, "end": v(729.3, 255.84) * mm});
            skLineSegment(sketch, "E125.0", {"start": v(729.3, 255.84) * mm, "end": v(729.3, 804.1) * mm});
            skSolve(sketch);
        }
        {
            var Q0;
            Q0 = qSketchRegion(id + "F40", true);
            var Q1;
            Q1=makeQuery(id+"F1.opExtrude","CAP_FACE",FACE,{"disambiguationData":[OSD([sQuery(id+"F0.wireOp",EDGE,"E0.bottom"),sQuery(id+"F0.wireOp",EDGE,"E0.top"),sQuery(id+"F0.wireOp",EDGE,"E0.left"),sQuery(id+"F0.wireOp",EDGE,"E0.right"),sQuery(id+"F0.wireOp",EDGE,"E1.bottom"),sQuery(id+"F0.wireOp",EDGE,"E1.top"),sQuery(id+"F0.wireOp",EDGE,"E1.left"),sQuery(id+"F0.wireOp",EDGE,"E1.right"),sQuery(id+"F0.wireOp",EDGE,"E2.bottom"),sQuery(id+"F0.wireOp",EDGE,"E2.top"),sQuery(id+"F0.wireOp",EDGE,"E2.left"),sQuery(id+"F0.wireOp",EDGE,"E2.right")])],"isStart":false});
            var Q2;
            Q2=makeQuery(id+"F1.opExtrude","CAP_FACE",FACE,{"disambiguationData":[OSD([sQuery(id+"F0.wireOp",EDGE,"E0.bottom"),sQuery(id+"F0.wireOp",EDGE,"E0.top"),sQuery(id+"F0.wireOp",EDGE,"E0.left"),sQuery(id+"F0.wireOp",EDGE,"E0.right"),sQuery(id+"F0.wireOp",EDGE,"E1.bottom"),sQuery(id+"F0.wireOp",EDGE,"E1.top"),sQuery(id+"F0.wireOp",EDGE,"E1.left"),sQuery(id+"F0.wireOp",EDGE,"E1.right"),sQuery(id+"F0.wireOp",EDGE,"E2.bottom"),sQuery(id+"F0.wireOp",EDGE,"E2.top"),sQuery(id+"F0.wireOp",EDGE,"E2.left"),sQuery(id+"F0.wireOp",EDGE,"E2.right")])],"isStart":true});
            extrude(context, id + "F41", {"entities" : qUnion([Q0]), "operationType" : NewBodyOperationType.ADD, "endBound" : BoundingType.UP_TO_SURFACE, "endBoundEntityFace" : qUnion([Q1]), "depth" : 25.4 * mm, "hasSecondDirection" : true, "secondDirectionBound" : SecondDirectionBoundingType.UP_TO_SURFACE, "secondDirectionOppositeDirection" : true, "secondDirectionBoundEntityFace" : qUnion([Q2]), "secondDirectionDepth" : 25.4 * mm});
        }
    });
